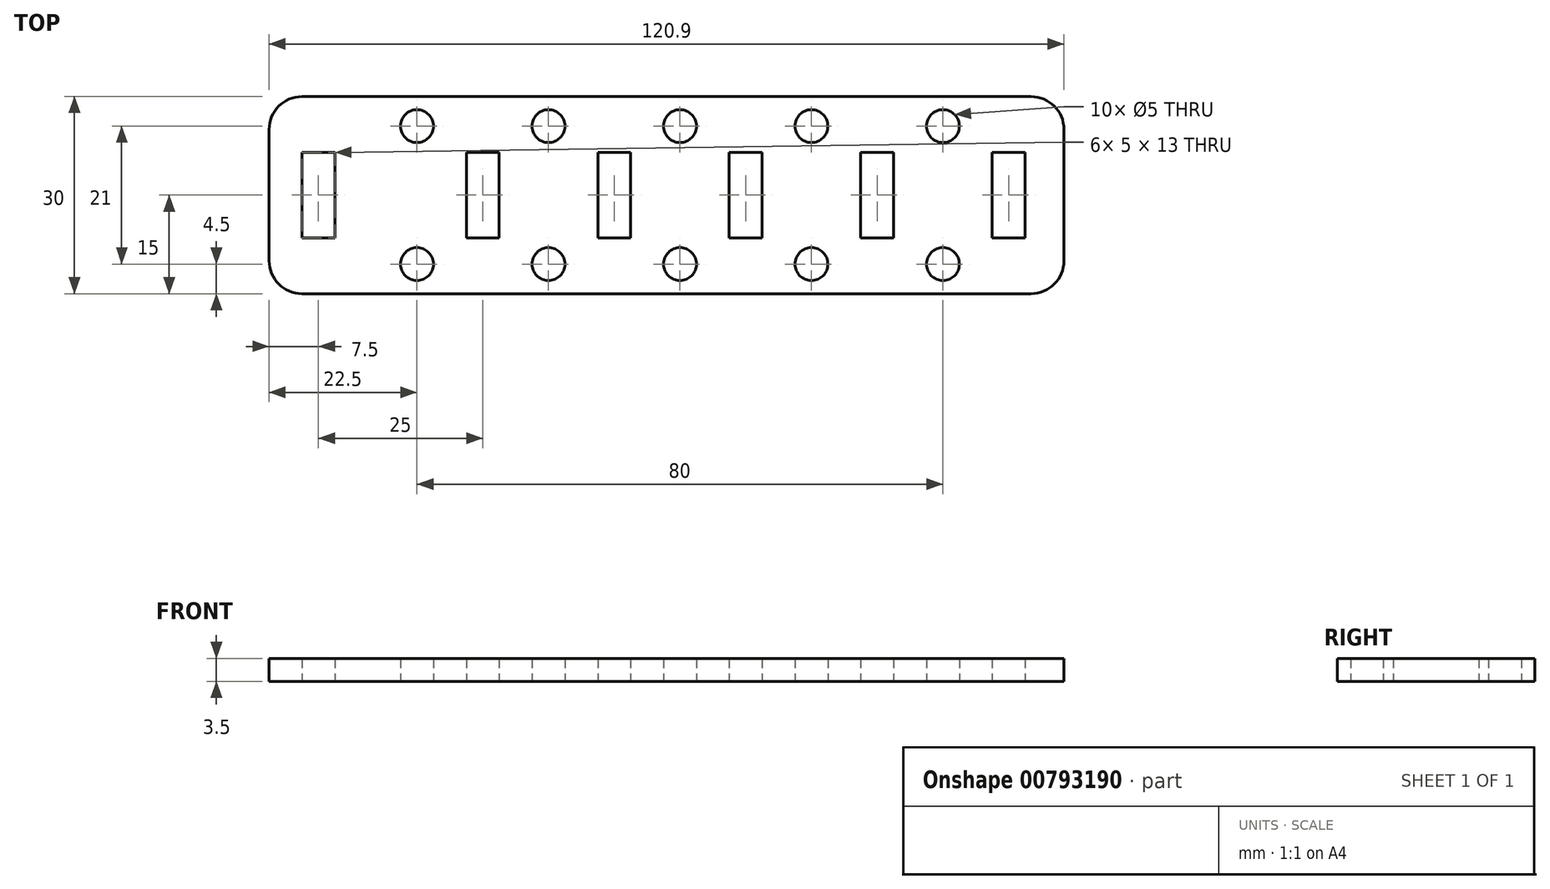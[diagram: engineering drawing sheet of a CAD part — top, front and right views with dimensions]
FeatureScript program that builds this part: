
annotation { "Feature Type Name" : "Feature", "Feature Type Description" : "" }
export const myFeature = defineFeature(function(context is Context, id is Id, definition is map)
    precondition{}
    {
        {
            var Q0;
            Q0=qCreatedBy(makeId("Top.planeOp"),FACE);
            var sketch = newSketch(context, id + "F0", { "sketchPlane" : qUnion([Q0])});
            skLineSegment(sketch, "E0.bottom", {"start": v(-5, 0) * mm, "end": v(-115.9, 0) * mm});
            skLineSegment(sketch, "E0.top", {"start": v(-5, -30) * mm, "end": v(-115.9, -30) * mm});
            skLineSegment(sketch, "E0.left", {"start": v(0, -5) * mm, "end": v(0, -25) * mm});
            skLineSegment(sketch, "E0.right", {"start": v(-120.9, 0) * mm, "end": v(-120.9, -30) * mm});
            skLineSegment(sketch, "E1", {"start": v(-120.9, -5) * mm, "end": v(-120.9, -8.5) * mm, "construction": true});
            skLineSegment(sketch, "E2", {"start": v(-120.9, -8.5) * mm, "end": v(-120.9, -21.5) * mm, "construction": true});
            skLineSegment(sketch, "E3", {"start": v(-120.9, -21.5) * mm, "end": v(-120.9, -25) * mm, "construction": true});
            skLineSegment(sketch, "E4", {"start": v(-120.9, -15) * mm, "end": v(-115.9, -15) * mm, "construction": true});
            skLineSegment(sketch, "E5.bottom", {"start": v(-115.9, -8.5) * mm, "end": v(-110.9, -8.5) * mm});
            skLineSegment(sketch, "E5.top", {"start": v(-115.9, -21.5) * mm, "end": v(-110.9, -21.5) * mm});
            skLineSegment(sketch, "E5.left", {"start": v(-115.9, -8.5) * mm, "end": v(-115.9, -21.5) * mm});
            skLineSegment(sketch, "E5.right", {"start": v(-110.9, -8.5) * mm, "end": v(-110.9, -21.5) * mm});
            skLineSegment(sketch, "E6.bottom", {"start": v(-90.9, -8.5) * mm, "end": v(-85.9, -8.5) * mm});
            skLineSegment(sketch, "E6.top", {"start": v(-90.9, -21.5) * mm, "end": v(-85.9, -21.5) * mm});
            skLineSegment(sketch, "E6.left", {"start": v(-90.9, -8.5) * mm, "end": v(-90.9, -21.5) * mm});
            skLineSegment(sketch, "E6.right", {"start": v(-85.9, -8.5) * mm, "end": v(-85.9, -21.5) * mm});
            skLineSegment(sketch, "E7.bottom", {"start": v(-70.9, -8.5) * mm, "end": v(-65.9, -8.5) * mm});
            skLineSegment(sketch, "E7.top", {"start": v(-70.9, -21.5) * mm, "end": v(-65.9, -21.5) * mm});
            skLineSegment(sketch, "E7.left", {"start": v(-70.9, -8.5) * mm, "end": v(-70.9, -21.5) * mm});
            skLineSegment(sketch, "E7.right", {"start": v(-65.9, -8.5) * mm, "end": v(-65.9, -21.5) * mm});
            skLineSegment(sketch, "E8.bottom", {"start": v(-50.9, -8.5) * mm, "end": v(-45.9, -8.5) * mm});
            skLineSegment(sketch, "E8.top", {"start": v(-50.9, -21.5) * mm, "end": v(-45.9, -21.5) * mm});
            skLineSegment(sketch, "E8.left", {"start": v(-50.9, -8.5) * mm, "end": v(-50.9, -21.5) * mm});
            skLineSegment(sketch, "E8.right", {"start": v(-45.9, -8.5) * mm, "end": v(-45.9, -21.5) * mm});
            skLineSegment(sketch, "E9.bottom", {"start": v(-10.9, -8.5) * mm, "end": v(-5.9, -8.5) * mm});
            skLineSegment(sketch, "E9.top", {"start": v(-10.9, -21.5) * mm, "end": v(-5.9, -21.5) * mm});
            skLineSegment(sketch, "E9.left", {"start": v(-10.9, -8.5) * mm, "end": v(-10.9, -21.5) * mm});
            skLineSegment(sketch, "E9.right", {"start": v(-5.9, -8.5) * mm, "end": v(-5.9, -21.5) * mm});
            skLineSegment(sketch, "E10.bottom", {"start": v(-30.9, -8.5) * mm, "end": v(-25.9, -8.5) * mm});
            skLineSegment(sketch, "E10.top", {"start": v(-30.9, -21.5) * mm, "end": v(-25.9, -21.5) * mm});
            skLineSegment(sketch, "E10.left", {"start": v(-30.9, -8.5) * mm, "end": v(-30.9, -21.5) * mm});
            skLineSegment(sketch, "E10.right", {"start": v(-25.9, -8.5) * mm, "end": v(-25.9, -21.5) * mm});
            skLineSegment(sketch, "E11", {"start": v(-85.9, -25.5) * mm, "end": v(-78.4, -25.5) * mm, "construction": true});
            skLineSegment(sketch, "E12", {"start": v(-78.4, -25.5) * mm, "end": v(-78.4, -30) * mm, "construction": true});
            skCircle(sketch, "E13", {"center": v(-78.4, -25.5) * mm, "radius": 2.5 * mm});
            skCircle(sketch, "E14", {"center": v(-58.4, -25.5) * mm, "radius": 2.5 * mm});
            skCircle(sketch, "E15", {"center": v(-38.4, -25.5) * mm, "radius": 2.5 * mm});
            skCircle(sketch, "E16", {"center": v(-18.4, -25.5) * mm, "radius": 2.5 * mm});
            skCircle(sketch, "E17", {"center": v(-98.4, -25.5) * mm, "radius": 2.5 * mm});
            skLineSegment(sketch, "E18.MirrorCS", {"start": v(-85.9, -4.5) * mm, "end": v(-78.4, -4.5) * mm, "construction": true});
            skCircle(sketch, "E19.MirrorC", {"center": v(-78.4, -4.5) * mm, "radius": 2.5 * mm});
            skCircle(sketch, "E20.MirrorC", {"center": v(-98.4, -4.5) * mm, "radius": 2.5 * mm});
            skLineSegment(sketch, "E21.MirrorCS", {"start": v(-78.4, -4.5) * mm, "end": v(-78.4, 0) * mm, "construction": true});
            skCircle(sketch, "E22.MirrorC", {"center": v(-18.4, -4.5) * mm, "radius": 2.5 * mm});
            skCircle(sketch, "E23.MirrorC", {"center": v(-58.4, -4.5) * mm, "radius": 2.5 * mm});
            skCircle(sketch, "E24.MirrorC", {"center": v(-38.4, -4.5) * mm, "radius": 2.5 * mm});
            skPoint(sketch, "E25.visualSharp", {"position": v(-120.9, 0) * mm});
            skArc(sketch, "E25.filletArc", {"start": v(-115.9, 0) * mm, "mid": v(-119.44, -1.46) * mm, "end": v(-120.9, -5) * mm});
            skPoint(sketch, "E26.visualSharp", {"position": v(-120.9, -30) * mm});
            skArc(sketch, "E26.filletArc", {"start": v(-120.9, -25) * mm, "mid": v(-119.44, -28.54) * mm, "end": v(-115.9, -30) * mm});
            skPoint(sketch, "E27.visualSharp", {"position": v(0, -30) * mm});
            skArc(sketch, "E27.filletArc", {"start": v(-5, -30) * mm, "mid": v(-1.46, -28.54) * mm, "end": v(0, -25) * mm});
            skPoint(sketch, "E28.visualSharp", {"position": v(0, 0) * mm});
            skArc(sketch, "E28.filletArc", {"start": v(0, -5) * mm, "mid": v(-1.46, -1.46) * mm, "end": v(-5, 0) * mm});
            skSolve(sketch);
        }
        {
            var Q0;
            Q0=makeQuery(id+"F0.imprint","IMPRINT",FACE,{"disambiguationData":[TD([[makeQuery(id+"F0.imprint","IMPRINT",EDGE,{"derivedFrom":sQuery(id+"F0.wireOp",EDGE,"E0.bottom")}),1.0]])]});
            extrude(context, id + "F1", {"entities" : qUnion([Q0]), "depth" : 3.5 * mm, "offsetDistance" : 25 * mm});
        }
    });
